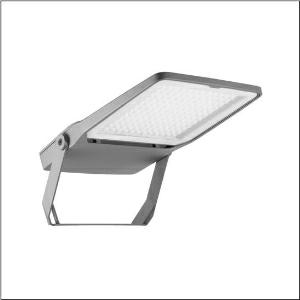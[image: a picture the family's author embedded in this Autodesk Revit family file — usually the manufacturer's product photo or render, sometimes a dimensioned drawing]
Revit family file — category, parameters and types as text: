
# Revit family: floodlight_fl_20_midi___pl43_5xa7681d2a1ac_811e
name_source: partatom
category: Lighting Fixtures
units: mm (PartAtom-declared; Revit-internal decimal feet)

## family parameters
Cut with Voids When Loaded = No
Host = Face
Light Source = No
Part Type = Normal
Room Calculation Point = No
Round Connector Dimension = Use Diameter
Shared = No

## types (1)
- Floodlight FL 20 midi  PL43 (1 x LED 4000K / CRI = 70 (unbekannt), 19080 lm, 4000K)
    Apparent Load = 142 VA
    CIE Flux Codes = 32 74 99 100 100
    Color Rendering = 70
    Color Temperature = 4000K
    Default Elevation = 1800 mm
    Description = Floodlight FL 20 midi, floodlight, primary light control with lens, of plastic, primary optical cover: protective disc, of toughened safety glass, transparent, light distribution: PL43, light emission: direct distribution, primary light characteristic: asymmetric, installation type: surface-mounted, LED, High Power LED, rated luminous flux: 19.080lm, luminous efficacy: 134lm/W, light colour: 740, colour temperature: 4000K, control gear: ECG Basic, control: power reduction, overheat protection, electronic power reduction, with terminal, 5-pole, max. 2.5mm², mains connection: 220..240V, AC, 50/60Hz, rated input power: 142W, LED unit, of diecast aluminium, powder-coated, Siteco® metallic grey (DB 702S), corrosivity category C5 mid according to DIN EN ISO 12944, incl. 1x M20 cable gland for cable Ø 6.5..12mm, length: 654mm, width: 450mm, height: 76mm, housing frame, of diecast aluminium, powder-coated, Siteco® metallic grey (DB 702S), mounting bracket, of steel, powder-coated, Siteco® metallic grey (DB 702S), ON/OFF, protection rating (complete): IP66, insulation class (complete): insulation class I (protective earthing), certification: CE, ENEC, VDE, protection symbol: D, permissible operating ambient temperature: -40..+40°C, permissible operating ambient temperature for outdoor applications: -40..+50°C, standard: DIN EN 12944, packaging unit: 1 piece

Light Distribution: PL43
    Height = 76 mm
    Lamp = 1 x LED 4000K / CRI >= 70 (unbekannt)
    Lamp Light Flux = 19080 lm
    Lamp count = 1
    Length = 672 mm
    Luminous efficacy = 134 lm/W
    Manufacturer = Siteco
    ModVariant = No
    Model = 5XA7681D2A1AC
    Mounting Place = Wall
    Mounting Type = Surface mounted
    Number of Poles = 1
    OnlyDefault = Yes
    Power Factor = 1
    Product Name = Floodlight FL 20 midi | PL43
    Product group = floodlight | wall mounted
    ProductGroupID = 2001
    Protection Class = Protection class I
    Protection Degree = IP 66
    RLX_Detail_Level = 1
    RLX_Emergency_Light_Flux = 0 lm
    RLX_Emergency_Type = 0
    RLX_Emergency_Type_DB = No
    RlxData = <blob elided: 94105 chars, md5=1739934f>
    Socket = socket
    Standby Power = 0 W
    System Light Flux = 19080 lm
    System Power = 142 W
    Type Comments = Product without accessories
    Type Image = l_1005943.jpg
    URL = http://relux.com
    VarID = ---
    Voltage = 0 V
    Weight = 0.00 kg
    Width = 450 mm

## geometry (parser evidence)
native form markers: Blend x4, Sweep x17
no freeform markers — native parametric forms only
